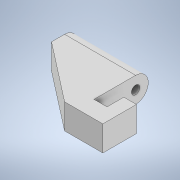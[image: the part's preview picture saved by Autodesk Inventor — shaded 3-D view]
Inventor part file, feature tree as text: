
AUTODESK INVENTOR PART (.ipt)
format: ipt  version: 2022 (Build 260153000, 153)  size: 133,632 bytes
history: native  units: in
note: dims shown in document units (in); Inventor stores cm internally (conversion verified against a paired STEP export)
features: extrude x3, sketch x3
ambient origin geometry x8: Origin, YZ Plane, XZ Plane, XY Plane, X Axis, Y Axis, Z Axis, Center Point
bodies: Solid1 (feature_tree)
feature tree (6):
  extrude  "Extrusion1"  Depth=0.6693in
  extrude  "Extrusion2"  Depth=0.1181in
  extrude  "Extrusion3"  Depth=0.3937in
  sketch  "Sketch1"  dims[d0=0.9055in d1=0.6693in]
  sketch  "Sketch2"  dims[d2=0.122in d3=0.1181in]
  sketch  "Sketch3"  dims[d4=0.1181in d5=0.2441in d6=0.2362in d7=0.0in d8=0.122in d9=0.0787in d10=0.2362in d11=0.0in d13=0.315in d14=0.3937in d15=0.0in d17=0.5118in]
